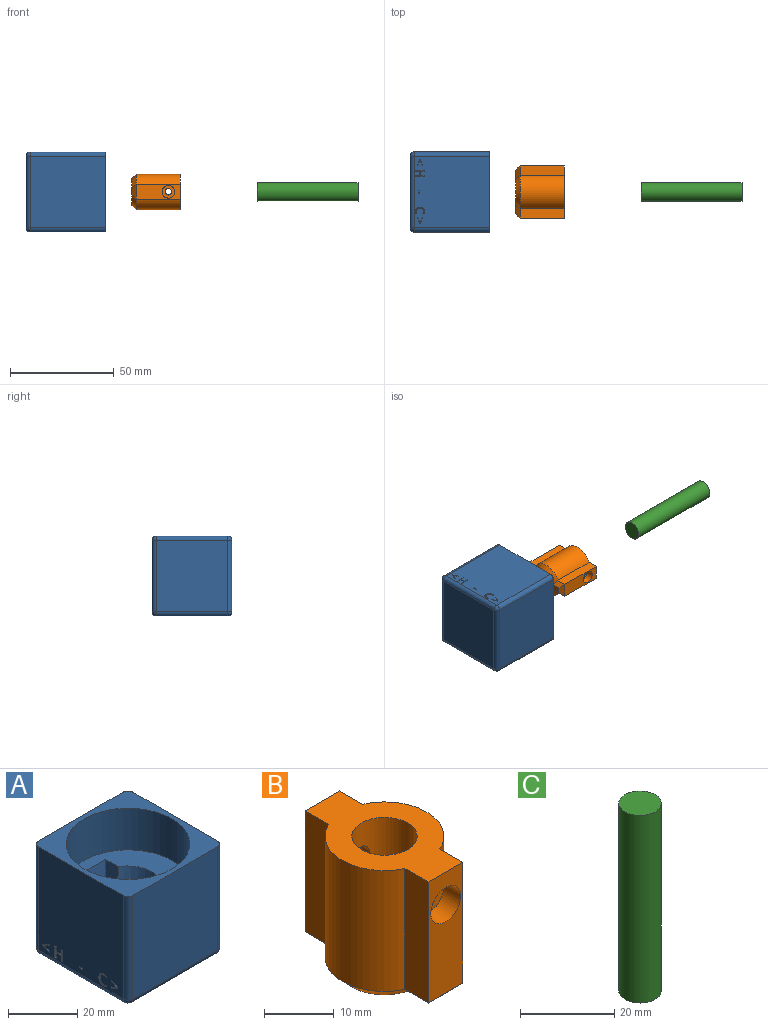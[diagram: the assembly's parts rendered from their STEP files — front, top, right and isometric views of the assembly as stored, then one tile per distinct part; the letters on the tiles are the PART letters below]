
ASSEMBLY  parts=3 mates=2
PART A: 137 faces, bbox 38.5x38.5x38.5 mm
  f0: plane 36.5x34.5mm, normal (-1,0,0), area 1246mm2, adj f14,f27,f33,f36,f87,f88,f89,f90
  f1: plane 36.5x34.5mm, normal (1,0,0), area 1246mm2, adj f14,f25,f29,f30,f37,f38,f39,f40
  f2: cylinder r=8.75mm len=17.13mm, axis (0,0,1), area 340.7mm2, adj f7,f10,f11,f22
  f3: plane 35.58x35.58mm, normal (0,0,1), area 614.2mm2, adj f15,f17,f18,f19,f20,f21,f22,f23
  f4: cylinder r=8.75mm len=17.13mm, axis (0,0,1), area 339mm2, adj f5,f9,f11,f19
  f5: plane 17.13x4.73mm, normal (1,0,0), area 81.1mm2, adj f4,f6,f11,f21
  f6: plane 17.13x7.4mm, normal (0,1,0), area 126.8mm2, adj f5,f7,f11,f23
  f7: plane 17.13x4.71mm, normal (-1,0,0), area 80.7mm2, adj f2,f6,f11,f24
  f8: plane 17.13x7.4mm, normal (0,-1,0), area 126.8mm2, adj f9,f10,f11,f18
  f9: plane 17.13x4.82mm, normal (1,0,0), area 82.6mm2, adj f4,f8,f11,f17
  f10: plane 17.13x4.8mm, normal (-1,0,0), area 82.2mm2, adj f2,f8,f11,f20
  f11: plane 25.39x17.5mm, normal (0,0,1), area 302.8mm2, adj f2,f4,f5,f6,f7,f8,f9,f10
  f12: plane 36.5x34.5mm, normal (0,-1,0), area 1259.2mm2, adj f14,f25,f27,f28
  f13: plane 36.5x34.5mm, normal (0,1,0), area 1259.2mm2, adj f14,f30,f34,f36
  f14: plane 38.5x38.5mm, normal (0,0,1), area 484.5mm2, adj f0,f1,f12,f13,f15,f25,f27,f30
  f15: cylinder r=17.79mm len=35.58mm, axis (0,0,1), area 1643.2mm2, adj f3,f14
  f16: plane 34.5x34.5mm, normal (0,0,-1), area 1190.2mm2, adj f28,f29,f33,f34
  f17: plane 5.82x5.67mm, normal (0.98,0,0.17), area 28.9mm2, adj f3,f9,f18,f19
  f18: plane 9.4x5.67mm, normal (0,-0.98,0.17), area 48.4mm2, adj f3,f8,f17,f20
  f19: cone r=8.75mm half-angle=10deg, axis (0,0,1), area 116.8mm2, adj f3,f4,f17,f21
  f20: plane 5.8x5.67mm, normal (-0.98,0,0.17), area 28.7mm2, adj f3,f10,f18,f22
  f21: plane 5.73x5.67mm, normal (0.98,0,0.17), area 28.4mm2, adj f3,f5,f19,f23
  f22: cone r=8.75mm half-angle=10deg, axis (0,0,1), area 117.4mm2, adj f2,f3,f20,f24
  f23: plane 9.4x5.67mm, normal (0,0.98,0.17), area 48.4mm2, adj f3,f6,f21,f24
  f24: plane 5.71x5.67mm, normal (-0.98,0,0.17), area 28.2mm2, adj f3,f7,f22,f23
  f25: cylinder r=2mm len=36.5mm, axis (0,0,1), area 114.7mm2, adj f1,f12,f14,f26
  f26: sphere r=2mm, area 6.3mm2, adj f25,f28,f29
  f27: cylinder r=2mm len=36.5mm, axis (0,0,-1), area 114.7mm2, adj f0,f12,f14,f31
  f28: cylinder r=2mm len=34.5mm, axis (1,0,0), area 108.4mm2, adj f12,f16,f26,f31
  f29: cylinder r=2mm len=34.5mm, axis (0,1,0), area 108.4mm2, adj f1,f16,f26,f32
  f30: cylinder r=2mm len=36.5mm, axis (0,0,-1), area 114.7mm2, adj f1,f13,f14,f32
  f31: sphere r=2mm, area 6.3mm2, adj f27,f28,f33
  f32: sphere r=2mm, area 6.3mm2, adj f29,f30,f34
  f33: cylinder r=2mm len=34.5mm, axis (0,-1,0), area 108.4mm2, adj f0,f16,f31,f35
  f34: cylinder r=2mm len=34.5mm, axis (-1,0,0), area 108.4mm2, adj f13,f16,f32,f35
  f35: sphere r=2mm, area 6.3mm2, adj f33,f34,f36
  f36: cylinder r=2mm len=36.5mm, axis (0,0,1), area 114.7mm2, adj f0,f13,f14,f35
  f37: plane 2.21x0.92mm, normal (0,0.38,-0.92), area 1.2mm2, adj f1,f38,f43,f44
  f38: plane 0.5x0.43mm, normal (0,1,0), area 0.2mm2, adj f1,f37,f39,f44
  f39: plane 2.71x1.19mm, normal (0,-0.4,0.92), area 1.5mm2, adj f1,f38,f40,f44
  f40: plane 0.5x0.28mm, normal (0,-1,0), area 0.1mm2, adj f1,f39,f41,f44
  f41: plane 2.71x1.35mm, normal (0,-0.45,-0.89), area 1.5mm2, adj f1,f40,f42,f44
  f42: plane 0.5x0.42mm, normal (0,1,0), area 0.2mm2, adj f1,f41,f43,f44
  f43: plane 2.21x1.05mm, normal (0,0.43,0.9), area 1.2mm2, adj f1,f37,f42,f44
  f44: plane 2.82x2.71mm, normal (1,0,0), area 2mm2, adj f37,f38,f39,f40,f41,f42,f43
  f45: extruded ~1.07x0.5mm, area 0.6mm2, adj f1,f46,f59,f60
  f46: extruded ~0.94x0.5mm, area 0.5mm2, adj f1,f45,f47,f60
  f47: plane 0.5x0.41mm, normal (0,-0.9,0.44), area 0.2mm2, adj f1,f46,f48,f60
  f48: extruded ~1.13x0.5mm, area 0.6mm2, adj f1,f47,f49,f60
  f49: extruded ~1.06x0.5mm, area 0.6mm2, adj f1,f48,f50,f60
  f50: extruded ~0.74x0.69mm, area 0.5mm2, adj f1,f49,f51,f60
  f51: extruded ~1.12x0.5mm, area 0.6mm2, adj f1,f50,f52,f60
  f52: extruded ~1.57x0.5mm, area 0.8mm2, adj f1,f51,f53,f60
  f53: extruded ~1.41x0.55mm, area 0.8mm2, adj f1,f52,f54,f60
  f54: extruded ~1.06x0.5mm, area 0.5mm2, adj f1,f53,f55,f60
  f55: plane 0.5x0.42mm, normal (0,-1,0), area 0.2mm2, adj f1,f54,f56,f60
  f56: extruded ~0.98x0.5mm, area 0.5mm2, adj f1,f55,f57,f60
  f57: extruded ~1.08x0.5mm, area 0.6mm2, adj f1,f56,f58,f60
  f58: extruded ~1.25x0.5mm, area 0.7mm2, adj f1,f57,f59,f60
  f59: extruded ~1.24x0.5mm, area 0.7mm2, adj f1,f45,f58,f60
  f60: plane 4.24x3.12mm, normal (1,0,0), area 3.7mm2, adj f45,f46,f47,f48,f49,f50,f51,f52
  f61: plane 0.5x0.43mm, normal (0,1,0), area 0.2mm2, adj f1,f62,f64,f65
  f62: plane 1.38x0.5mm, normal (0,0,1), area 0.7mm2, adj f1,f61,f63,f65
  f63: plane 0.5x0.43mm, normal (0,-1,0), area 0.2mm2, adj f1,f62,f64,f65
  f64: plane 1.38x0.5mm, normal (0,0,-1), area 0.7mm2, adj f1,f61,f63,f65
  f65: plane 1.38x0.43mm, normal (1,0,0), area 0.6mm2, adj f61,f62,f63,f64
  f66: plane 0.5x0.48mm, normal (0,0,1), area 0.2mm2, adj f1,f67,f77,f78
  f67: plane 4.12x0.5mm, normal (0,-1,0), area 2.1mm2, adj f1,f66,f68,f78
  f68: plane 0.5x0.48mm, normal (0,0,-1), area 0.2mm2, adj f1,f67,f69,f78
  f69: plane 1.75x0.5mm, normal (0,1,0), area 0.9mm2, adj f1,f68,f70,f78
  f70: plane 2.17x0.5mm, normal (0,0,-1), area 1.1mm2, adj f1,f69,f71,f78
  f71: plane 1.75x0.5mm, normal (0,-1,0), area 0.9mm2, adj f1,f70,f72,f78
  f72: plane 0.5x0.48mm, normal (0,0,-1), area 0.2mm2, adj f1,f71,f73,f78
  f73: plane 4.12x0.5mm, normal (0,1,0), area 2.1mm2, adj f1,f72,f74,f78
  f74: plane 0.5x0.48mm, normal (0,0,1), area 0.2mm2, adj f1,f73,f75,f78
  f75: plane 1.94x0.5mm, normal (0,-1,0), area 1mm2, adj f1,f74,f76,f78
  f76: plane 2.17x0.5mm, normal (0,0,1), area 1.1mm2, adj f1,f75,f77,f78
  f77: plane 1.94x0.5mm, normal (0,1,0), area 1mm2, adj f1,f66,f76,f78
  f78: plane 4.12x3.13mm, normal (1,0,0), area 4.9mm2, adj f66,f67,f68,f69,f70,f71,f72,f73
  f79: plane 2.71x1.19mm, normal (0,0.4,0.92), area 1.5mm2, adj f1,f80,f85,f86
  f80: plane 0.5x0.43mm, normal (0,-1,0), area 0.2mm2, adj f1,f79,f81,f86
  f81: plane 2.2x0.92mm, normal (0,-0.39,-0.92), area 1.2mm2, adj f1,f80,f82,f86
  f82: plane 2.2x1.05mm, normal (0,-0.43,0.9), area 1.2mm2, adj f1,f81,f83,f86
  f83: plane 0.5x0.42mm, normal (0,-1,0), area 0.2mm2, adj f1,f82,f84,f86
  f84: plane 2.71x1.35mm, normal (0,0.45,-0.89), area 1.5mm2, adj f1,f83,f85,f86
  f85: plane 0.5x0.28mm, normal (0,1,0), area 0.1mm2, adj f1,f79,f84,f86
  f86: plane 2.82x2.71mm, normal (1,0,0), area 2mm2, adj f79,f80,f81,f82,f83,f84,f85
  f87: plane 2.21x0.92mm, normal (0,-0.38,-0.92), area 1.2mm2, adj f0,f88,f93,f94
  f88: plane 0.5x0.43mm, normal (0,-1,0), area 0.2mm2, adj f0,f87,f89,f94
  f89: plane 2.71x1.19mm, normal (0,0.4,0.92), area 1.5mm2, adj f0,f88,f90,f94
  f90: plane 0.5x0.28mm, normal (0,1,0), area 0.1mm2, adj f0,f89,f91,f94
  f91: plane 2.71x1.35mm, normal (0,0.45,-0.89), area 1.5mm2, adj f0,f90,f92,f94
  f92: plane 0.5x0.42mm, normal (0,-1,0), area 0.2mm2, adj f0,f91,f93,f94
  f93: plane 2.21x1.05mm, normal (0,-0.43,0.9), area 1.2mm2, adj f0,f87,f92,f94
  f94: plane 2.82x2.71mm, normal (-1,0,0), area 2mm2, adj f87,f88,f89,f90,f91,f92,f93
  f95: extruded ~1.07x0.5mm, area 0.6mm2, adj f0,f96,f109,f110
  f96: extruded ~0.94x0.5mm, area 0.5mm2, adj f0,f95,f97,f110
  f97: plane 0.5x0.41mm, normal (0,0.9,0.44), area 0.2mm2, adj f0,f96,f98,f110
  f98: extruded ~1.13x0.5mm, area 0.6mm2, adj f0,f97,f99,f110
  f99: extruded ~1.06x0.5mm, area 0.6mm2, adj f0,f98,f100,f110
  f100: extruded ~0.74x0.69mm, area 0.5mm2, adj f0,f99,f101,f110
  f101: extruded ~1.12x0.5mm, area 0.6mm2, adj f0,f100,f102,f110
  f102: extruded ~1.57x0.5mm, area 0.8mm2, adj f0,f101,f103,f110
  f103: extruded ~1.41x0.55mm, area 0.8mm2, adj f0,f102,f104,f110
  f104: extruded ~1.06x0.5mm, area 0.5mm2, adj f0,f103,f105,f110
  f105: plane 0.5x0.42mm, normal (0,1,0), area 0.2mm2, adj f0,f104,f106,f110
  f106: extruded ~0.98x0.5mm, area 0.5mm2, adj f0,f105,f107,f110
  f107: extruded ~1.08x0.5mm, area 0.6mm2, adj f0,f106,f108,f110
  f108: extruded ~1.25x0.5mm, area 0.7mm2, adj f0,f107,f109,f110
  f109: extruded ~1.24x0.5mm, area 0.7mm2, adj f0,f95,f108,f110
  f110: plane 4.24x3.12mm, normal (-1,0,0), area 3.7mm2, adj f95,f96,f97,f98,f99,f100,f101,f102
  f111: plane 0.5x0.43mm, normal (0,-1,0), area 0.2mm2, adj f0,f112,f114,f115
  f112: plane 1.38x0.5mm, normal (0,0,1), area 0.7mm2, adj f0,f111,f113,f115
  f113: plane 0.5x0.43mm, normal (0,1,0), area 0.2mm2, adj f0,f112,f114,f115
  f114: plane 1.38x0.5mm, normal (0,0,-1), area 0.7mm2, adj f0,f111,f113,f115
  f115: plane 1.38x0.43mm, normal (-1,0,0), area 0.6mm2, adj f111,f112,f113,f114
  f116: plane 0.5x0.48mm, normal (0,0,1), area 0.2mm2, adj f0,f117,f127,f128
  f117: plane 4.12x0.5mm, normal (0,1,0), area 2.1mm2, adj f0,f116,f118,f128
  f118: plane 0.5x0.48mm, normal (0,0,-1), area 0.2mm2, adj f0,f117,f119,f128
  f119: plane 1.75x0.5mm, normal (0,-1,0), area 0.9mm2, adj f0,f118,f120,f128
  f120: plane 2.17x0.5mm, normal (0,0,-1), area 1.1mm2, adj f0,f119,f121,f128
  f121: plane 1.75x0.5mm, normal (0,1,0), area 0.9mm2, adj f0,f120,f122,f128
  f122: plane 0.5x0.48mm, normal (0,0,-1), area 0.2mm2, adj f0,f121,f123,f128
  f123: plane 4.12x0.5mm, normal (0,-1,0), area 2.1mm2, adj f0,f122,f124,f128
  f124: plane 0.5x0.48mm, normal (0,0,1), area 0.2mm2, adj f0,f123,f125,f128
  f125: plane 1.94x0.5mm, normal (0,1,0), area 1mm2, adj f0,f124,f126,f128
  f126: plane 2.17x0.5mm, normal (0,0,1), area 1.1mm2, adj f0,f125,f127,f128
  f127: plane 1.94x0.5mm, normal (0,-1,0), area 1mm2, adj f0,f116,f126,f128
  f128: plane 4.12x3.13mm, normal (-1,0,0), area 4.9mm2, adj f116,f117,f118,f119,f120,f121,f122,f123
  f129: plane 2.71x1.19mm, normal (0,-0.4,0.92), area 1.5mm2, adj f0,f130,f135,f136
  f130: plane 0.5x0.43mm, normal (0,1,0), area 0.2mm2, adj f0,f129,f131,f136
  f131: plane 2.2x0.92mm, normal (0,0.39,-0.92), area 1.2mm2, adj f0,f130,f132,f136
  f132: plane 2.2x1.05mm, normal (0,0.43,0.9), area 1.2mm2, adj f0,f131,f133,f136
  f133: plane 0.5x0.42mm, normal (0,1,0), area 0.2mm2, adj f0,f132,f134,f136
  f134: plane 2.71x1.35mm, normal (0,-0.45,-0.89), area 1.5mm2, adj f0,f133,f135,f136
  f135: plane 0.5x0.28mm, normal (0,-1,0), area 0.1mm2, adj f0,f129,f134,f136
  f136: plane 2.82x2.71mm, normal (-1,0,0), area 2mm2, adj f129,f130,f131,f132,f133,f134,f135
PART B: 31 faces, bbox 17.3x25.3x23.5 mm
  f0: cylinder r=1.55mm len=5.86mm, axis (0,-1,0), area 55.4mm2, adj f5,f30
  f1: cylinder r=1.55mm len=4.76mm, axis (0,-1,0), area 44.7mm2, adj f5,f23
  f2: cylinder r=8.56mm len=21.3mm, axis (0,0,-1), area 414.4mm2, adj f4,f10,f11,f21
  f3: cylinder r=8.56mm len=21.3mm, axis (0,0,-1), area 423.8mm2, adj f4,f9,f12,f14
  f4: plane 25.12x17.12mm, normal (0,0,1), area 220.2mm2, adj f2,f3,f5,f8,f9,f10,f11,f12
  f5: cylinder r=4.7mm len=13mm, axis (0,0,1), area 368.6mm2, adj f0,f1,f4,f6
  f6: plane 9.4x9.4mm, normal (0,0,1), area 69.4mm2, adj f5
  f7: plane 21.12x13.12mm, normal (0,0,-1), area 159.5mm2, adj f14,f15,f16,f17,f18,f19,f20,f21
  f8: plane 21.3x7mm, normal (0,-1,0), area 120.2mm2, adj f4,f9,f10,f18,f22
  f9: plane 21.3x4.7mm, normal (1,0,0), area 100.2mm2, adj f3,f4,f8,f16
  f10: plane 21.3x4.79mm, normal (-1,0,0), area 102.1mm2, adj f2,f4,f8,f20
  f11: plane 21.3x4.79mm, normal (-1,0,0), area 102.1mm2, adj f2,f4,f13,f19
  f12: plane 21.3x4.7mm, normal (1,0,0), area 100.2mm2, adj f3,f4,f13,f15
  f13: plane 21.3x7mm, normal (0,1,0), area 121.9mm2, adj f4,f11,f12,f17,f24,f25,f26,f27
  f14: cone r=8.56mm half-angle=45deg, axis (0,0,1), area 53.7mm2, adj f3,f7,f15,f16
  f15: plane 6.31x2.16mm, normal (0.71,0,-0.71), area 12.5mm2, adj f7,f12,f14,f17
  f16: plane 6.31x2.16mm, normal (0.71,0,-0.71), area 12.5mm2, adj f7,f9,f14,f18
  f17: plane 7x2mm, normal (0,0.71,-0.71), area 14.1mm2, adj f7,f13,f15,f19
  f18: plane 7x2mm, normal (0,-0.71,-0.71), area 14.1mm2, adj f7,f8,f16,f20
  f19: plane 6.35x2.15mm, normal (-0.71,0,-0.71), area 12.7mm2, adj f7,f11,f17,f21
  f20: plane 6.35x2.15mm, normal (-0.71,0,-0.71), area 12.7mm2, adj f7,f10,f18,f21
  f21: cone r=8.56mm half-angle=45deg, axis (0,0,1), area 52.4mm2, adj f2,f7,f19,f20
  f22: cylinder r=3.03mm len=6.06mm, axis (0,-1,0), area 64.7mm2, adj f8,f23
  f23: plane 6.06x6.06mm, normal (0,-1,0), area 21.3mm2, adj f1,f22
  f24: plane 2.81x2.3mm, normal (-0.49,0,0.87), area 7.4mm2, adj f13,f25,f29,f30
  f25: plane 2.79x2.3mm, normal (0.51,0,0.86), area 7.4mm2, adj f13,f24,f26,f30
  f26: plane 3.23x2.3mm, normal (1,0,-0.01), area 7.4mm2, adj f13,f25,f27,f30
  f27: plane 2.81x2.3mm, normal (0.49,0,-0.87), area 7.4mm2, adj f13,f26,f28,f30
  f28: plane 2.79x2.3mm, normal (-0.51,0,-0.86), area 7.4mm2, adj f13,f27,f29,f30
  f29: plane 3.23x2.3mm, normal (-1,0,0.01), area 7.4mm2, adj f13,f24,f28,f30
  f30: plane 6.47x5.62mm, normal (0,1,0), area 19.6mm2, adj f0,f24,f25,f26,f27,f28,f29
PART C: 3 faces, bbox 9x9x48.6 mm
  f0: cylinder r=4.5mm len=48.6mm, axis (0,0,-1), area 1374.1mm2, adj f1,f2
  f1: plane 9x9mm, normal (0,0,1), area 63.6mm2, adj f0
  f2: plane 9x9mm, normal (0,0,-1), area 63.6mm2, adj f0
PLACE A rot(axis=(0,1,0),90deg) t=(-190.79,3.22,137.6)mm fixed
PLACE B rot(axis=(0,1,0),90deg) t=(-140.79,3.22,137.6)mm
PLACE C rot(axis=(0,-1,0),90deg) t=(-30.89,8.45,139.04)mm
MATE slider B.f2 <-> C.f0  axis (1,0,0) through (-129.49,8.45,139.04)mm
MATE slider B.f2 <-> A.f2  axis (-1,0,0) through (-139.79,8.45,139.04)mm
